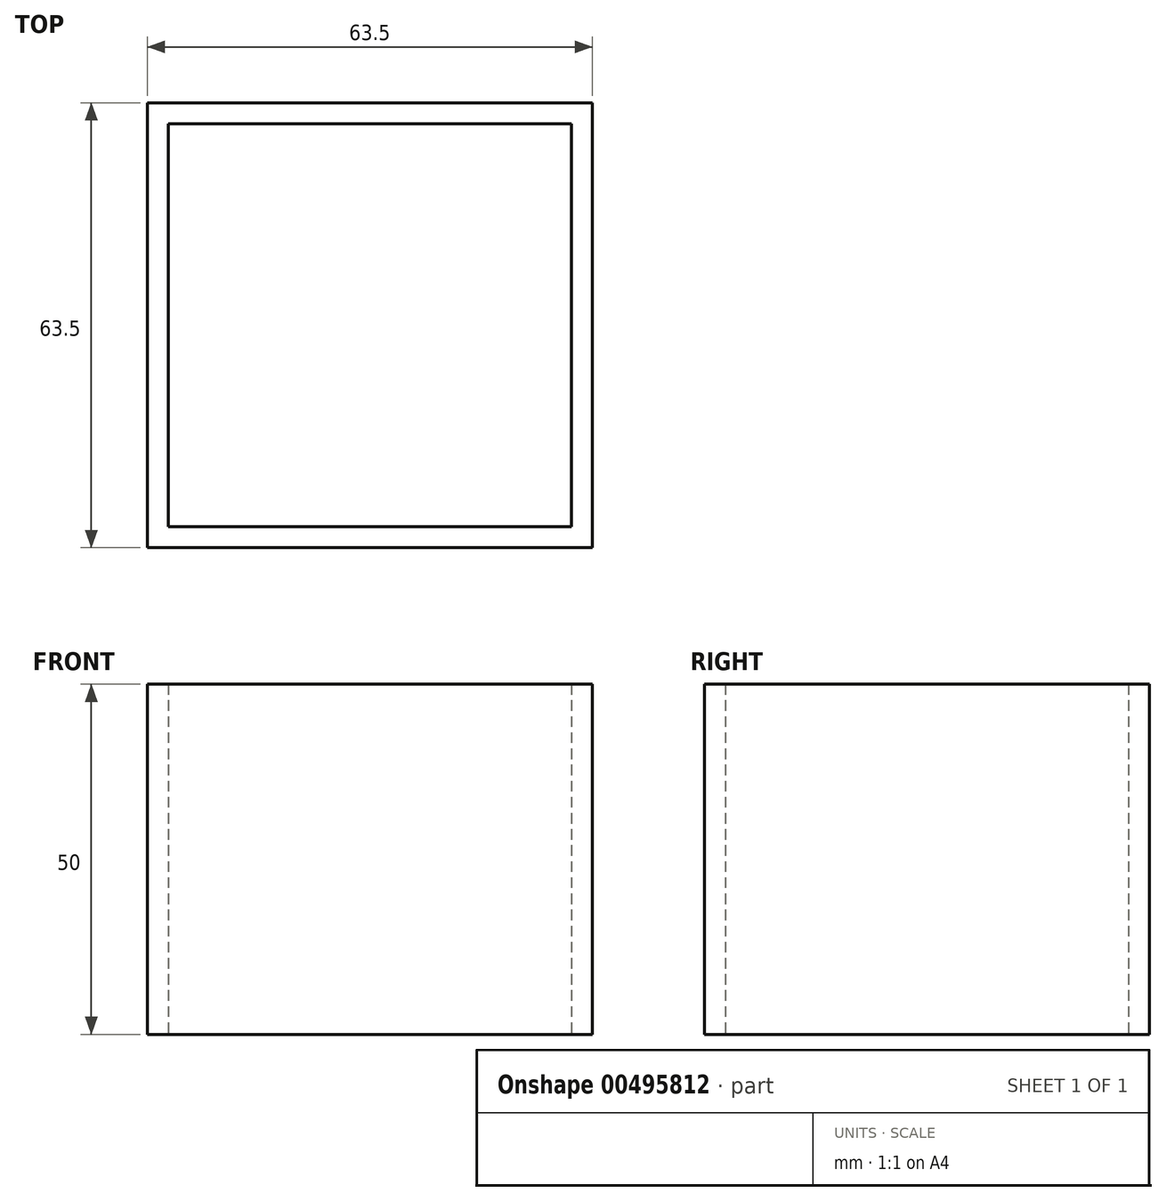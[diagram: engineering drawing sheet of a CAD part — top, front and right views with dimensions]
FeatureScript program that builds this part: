
annotation { "Feature Type Name" : "Feature", "Feature Type Description" : "" }
export const myFeature = defineFeature(function(context is Context, id is Id, definition is map)
    precondition{}
    {
        {
            var Q0;
            Q0=qCreatedBy(makeId("Top.planeOp"),FACE);
            var sketch = newSketch(context, id + "F0", { "sketchPlane" : qUnion([Q0])});
            skLineSegment(sketch, "E0.bottom", {"start": v(-27.29, 27.59) * mm, "end": v(36.21, 27.59) * mm});
            skLineSegment(sketch, "E0.top", {"start": v(-27.29, -35.91) * mm, "end": v(36.21, -35.91) * mm});
            skLineSegment(sketch, "E0.left", {"start": v(-27.29, 27.59) * mm, "end": v(-27.29, -35.91) * mm});
            skLineSegment(sketch, "E0.right", {"start": v(36.21, 27.59) * mm, "end": v(36.21, -35.91) * mm});
            skLineSegment(sketch, "E1.bottom", {"start": v(-24.29, 24.59) * mm, "end": v(33.21, 24.59) * mm});
            skLineSegment(sketch, "E1.top", {"start": v(-24.29, -32.91) * mm, "end": v(33.21, -32.91) * mm});
            skLineSegment(sketch, "E1.left", {"start": v(-24.29, 24.59) * mm, "end": v(-24.29, -32.91) * mm});
            skLineSegment(sketch, "E1.right", {"start": v(33.21, 24.59) * mm, "end": v(33.21, -32.91) * mm});
            skSolve(sketch);
        }
        {
            var Q0;
            Q0=qSketchRegion(id+"F0",true);
            extrude(context, id + "F1", {"entities" : qUnion([Q0]), "depth" : 50 * mm});
        }
    });
